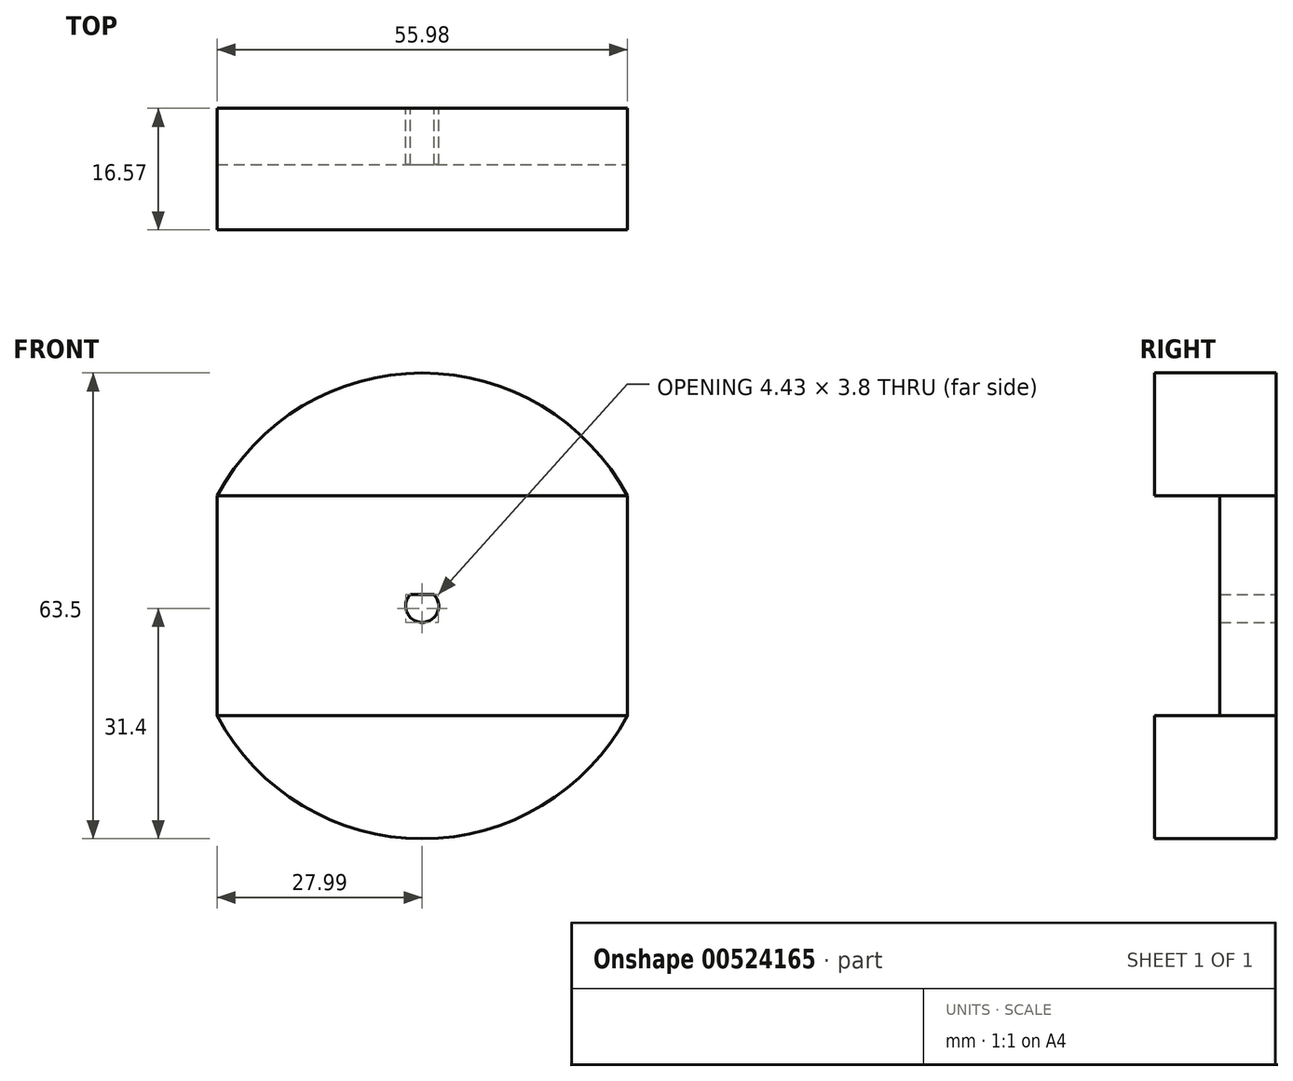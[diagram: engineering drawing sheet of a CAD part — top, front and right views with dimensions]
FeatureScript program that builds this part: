
annotation { "Feature Type Name" : "Feature", "Feature Type Description" : "" }
export const myFeature = defineFeature(function(context is Context, id is Id, definition is map)
    precondition{}
    {
        {
            var Q0;
            Q0=qCreatedBy(makeId("Front.planeOp"),FACE);
            var sketch = newSketch(context, id + "F0", { "sketchPlane" : qUnion([Q0])});
            skCircle(sketch, "E0", {"center": v(0, 0) * mm, "radius": 31.75 * mm});
            skCircle(sketch, "E1", {"center": v(0, 0) * mm, "radius": 2.25 * mm});
            skSolve(sketch);
        }
        {
            var Q0;
            Q0=qSketchRegion(id+"F0",true);
            extrude(context, id + "F1", {"entities" : qUnion([Q0]), "depth" : 4 * mm});
        }
        {
            var Q0;
            Q0=makeQuery(id+"F1.opExtrude","CAP_FACE",FACE,{"disambiguationData":[OSD([sQuery(id+"F0.wireOp",EDGE,"E0"),sQuery(id+"F0.wireOp",EDGE,"E1")])],"isStart":false});
            var sketch = newSketch(context, id + "F2", { "sketchPlane" : qUnion([Q0])});
            skCircle(sketch, "E2", {"center": v(0, 0) * mm, "radius": 31.75 * mm});
            skLineSegment(sketch, "E3", {"start": v(-1.63, 1.55) * mm, "end": v(1.63, 1.55) * mm});
            skArc(sketch, "E4", {"start": v(1.63, 1.55) * mm, "mid": v(0, 2.25) * mm, "end": v(-1.63, 1.55) * mm});
            skSolve(sketch);
        }
        {
            var Q0;
            Q0=makeQuery(id+"F2.imprint","IMPRINT",FACE,{"disambiguationData":[TD([[makeQuery(id+"F2.imprint","IMPRINT",EDGE,{"derivedFrom":sQuery(id+"F2.wireOp",EDGE,"E2")}),1.0]])]});
            var Q1;
            Q1=makeQuery(id+"F2.imprint","IMPRINT",FACE,{"disambiguationData":[TD([[makeQuery(id+"F2.imprint","IMPRINT",EDGE,{"derivedFrom":sQuery(id+"F2.wireOp",EDGE,"E3")}),1.0]])]});
            extrude(context, id + "F3", {"entities" : qUnion([Q0, Q1]), "operationType" : NewBodyOperationType.ADD, "depth" : 8 * mm});
        }
        {
            var Q0;
            Q0=makeQuery(id+"F3.opExtrude","CAP_FACE",FACE,{"disambiguationData":[OSD([sQuery(id+"F0.wireOp",EDGE,"E1"),sQuery(id+"F2.wireOp",EDGE,"E2"),sQuery(id+"F2.wireOp",EDGE,"E3")])],"isStart":false});
            var sketch = newSketch(context, id + "F4", { "sketchPlane" : qUnion([Q0])});
            skLineSegment(sketch, "E5", {"start": v(-28, 14.99) * mm, "end": v(-28, -14.99) * mm});
            skLineSegment(sketch, "E6", {"start": v(28, 14.99) * mm, "end": v(28, -14.99) * mm});
            skLineSegment(sketch, "E7", {"start": v(-28, 14.99) * mm, "end": v(28, 14.99) * mm});
            skLineSegment(sketch, "E8", {"start": v(28, -14.99) * mm, "end": v(-28, -14.99) * mm});
            skSolve(sketch);
        }
        {
            var Q0;
            {var subQ0=sQuery(id+"F4.wireOp",EDGE,"E7");Q0=makeQuery(id+"F4.imprint","IMPRINT",FACE,{"disambiguationData":[TD([[makeQuery(id+"F4.imprint","IMPRINT",EDGE,{"derivedFrom":subQ0}),1.0]])]});}
            var Q1;
            {var subQ0=sQuery(id+"F4.wireOp",EDGE,"E8");Q1=makeQuery(id+"F4.imprint","IMPRINT",FACE,{"disambiguationData":[TD([[makeQuery(id+"F4.imprint","IMPRINT",EDGE,{"derivedFrom":subQ0}),1.0]])]});}
            extrude(context, id + "F5", {"entities" : qUnion([Q0, Q1]), "operationType" : NewBodyOperationType.ADD, "depth" : 8.9 * mm});
        }
        {
            var Q0;
            Q0=makeQuery(id+"F5.opExtrude","CAP_FACE",FACE,{"disambiguationData":[OSD([sQuery(id+"F2.wireOp",EDGE,"E2"),sQuery(id+"F4.wireOp",EDGE,"E7")])],"isStart":false});
            var sketch = newSketch(context, id + "F6", { "sketchPlane" : qUnion([Q0])});
            skCircle(sketch, "E9", {"center": v(0, 0) * mm, "radius": 31.75 * mm});
            skLineSegment(sketch, "E10", {"start": v(-28, 14.99) * mm, "end": v(-28, -14.99) * mm});
            skLineSegment(sketch, "E11", {"start": v(28, 14.99) * mm, "end": v(28, -14.99) * mm});
            skSolve(sketch);
        }
        {
            var Q0;
            {var subQ0=sQuery(id+"F6.wireOp",EDGE,"E10");Q0=makeQuery(id+"F6.imprint","IMPRINT",FACE,{"disambiguationData":[TD([[makeQuery(id+"F6.imprint","IMPRINT",EDGE,{"derivedFrom":subQ0}),-1.0]])]});}
            var Q1;
            {var subQ0=sQuery(id+"F6.wireOp",EDGE,"E11");Q1=makeQuery(id+"F6.imprint","IMPRINT",FACE,{"disambiguationData":[TD([[makeQuery(id+"F6.imprint","IMPRINT",EDGE,{"derivedFrom":subQ0}),1.0]])]});}
            extrude(context, id + "F7", {"entities" : qUnion([Q0, Q1]), "operationType" : NewBodyOperationType.REMOVE, "endBound" : BoundingType.THROUGH_ALL, "oppositeDirection" : true, "depth" : 25.4 * mm});
        }
        {
            var Q0;
            Q0=makeQuery(id+"F1.opExtrude","CAP_FACE",FACE,{"disambiguationData":[OSD([sQuery(id+"F0.wireOp",EDGE,"E0"),sQuery(id+"F0.wireOp",EDGE,"E1")])],"isStart":true});
            var sketch = newSketch(context, id + "F8", { "sketchPlane" : qUnion([Q0])});
            skCircle(sketch, "E12", {"center": v(0, 0) * mm, "radius": 39.7 * mm});
            skSolve(sketch);
        }
        {
            var Q0;
            Q0=qSketchRegion(id+"F8",true);
            extrude(context, id + "F9", {"entities" : qUnion([Q0]), "operationType" : NewBodyOperationType.REMOVE, "oppositeDirection" : true, "depth" : 4.32 * mm});
        }
    });
